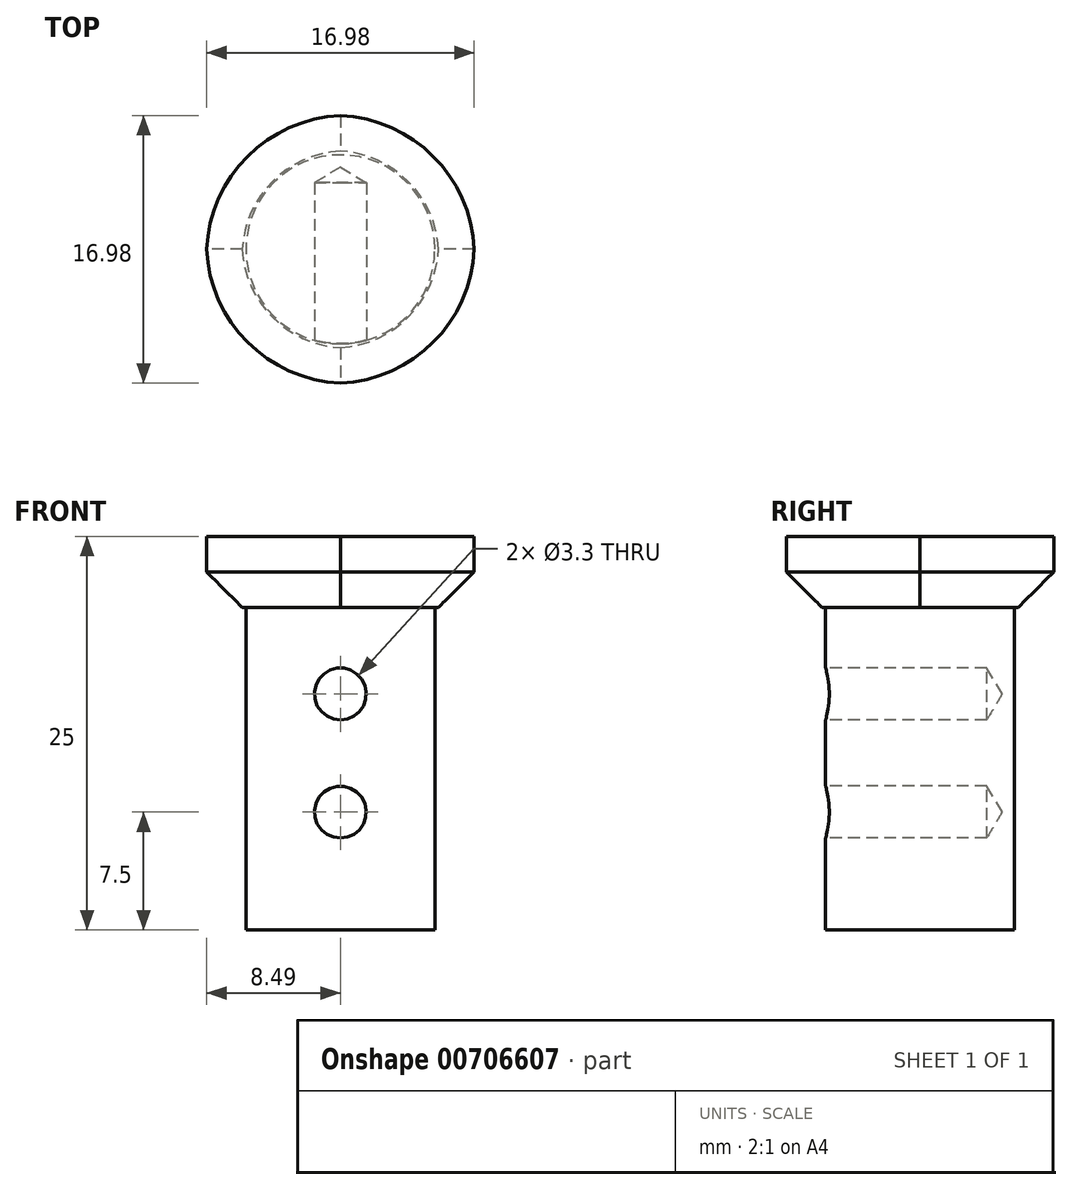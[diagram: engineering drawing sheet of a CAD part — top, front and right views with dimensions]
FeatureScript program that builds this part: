
annotation { "Feature Type Name" : "Feature", "Feature Type Description" : "" }
export const myFeature = defineFeature(function(context is Context, id is Id, definition is map)
    precondition{}
    {
        {
            var Q0;
            Q0=qCreatedBy(makeId("Top.planeOp"),FACE);
            var sketch = newSketch(context, id + "F0", { "sketchPlane" : qUnion([Q0])});
            skLineSegment(sketch, "E0.bottom", {"start": v(8.5, 8.5) * mm, "end": v(-8.5, 8.5) * mm});
            skLineSegment(sketch, "E0.top", {"start": v(8.5, -8.5) * mm, "end": v(-8.5, -8.5) * mm});
            skLineSegment(sketch, "E0.left", {"start": v(8.5, 8.5) * mm, "end": v(8.5, -8.5) * mm});
            skLineSegment(sketch, "E0.right", {"start": v(-8.5, 8.5) * mm, "end": v(-8.5, -8.5) * mm});
            skPoint(sketch, "E0.middle", {"position": v(0, 0) * mm});
            skLineSegment(sketch, "E1.bottom", {"start": v(0, 6) * mm, "end": v(0, 6) * mm});
            skLineSegment(sketch, "E1.top", {"start": v(0, -6) * mm, "end": v(0, -6) * mm});
            skLineSegment(sketch, "E1.left", {"start": v(6, 0) * mm, "end": v(6, 0) * mm});
            skLineSegment(sketch, "E1.right", {"start": v(-6, 0) * mm, "end": v(-6, 0) * mm});
            skPoint(sketch, "E2.visualSharp", {"position": v(-6, -6) * mm});
            skArc(sketch, "E2.filletArc", {"start": v(-6, 0) * mm, "mid": v(-4.24, -4.24) * mm, "end": v(0, -6) * mm});
            skPoint(sketch, "E3.visualSharp", {"position": v(6, -6) * mm});
            skArc(sketch, "E3.filletArc", {"start": v(0, -6) * mm, "mid": v(4.24, -4.24) * mm, "end": v(6, 0) * mm});
            skPoint(sketch, "E4.visualSharp", {"position": v(6, 6) * mm});
            skArc(sketch, "E4.filletArc", {"start": v(6, 0) * mm, "mid": v(4.24, 4.24) * mm, "end": v(0, 6) * mm});
            skPoint(sketch, "E5.visualSharp", {"position": v(-6, 6) * mm});
            skArc(sketch, "E5.filletArc", {"start": v(0, 6) * mm, "mid": v(-4.24, 4.24) * mm, "end": v(-6, 0) * mm});
            skCircle(sketch, "E6", {"center": v(0, 0) * mm, "radius": 8.5 * mm});
            skSolve(sketch);
        }
        {
            var Q0;
            Q0=makeQuery(id+"F0.imprint","IMPRINT",FACE,{"disambiguationData":[TD([[makeQuery(id+"F0.imprint","IMPRINT",EDGE,{"derivedFrom":sQuery(id+"F0.wireOp",EDGE,"E0.bottom")}),1.0]])]});
            var Q1;
            Q1=makeQuery(id+"F0.imprint","IMPRINT",FACE,{"disambiguationData":[TD([[makeQuery(id+"F0.imprint","IMPRINT",EDGE,{"derivedFrom":sQuery(id+"F0.wireOp",EDGE,"E2.filletArc")}),1.0]])]});
            var Q2;
            Q2=makeQuery(id+"F0.imprint","IMPRINT",FACE,{"disambiguationData":[TD([[makeQuery(id+"F0.imprint","IMPRINT",EDGE,{"derivedFrom":sQuery(id+"F0.wireOp",EDGE,"E2.filletArc")}),-1.0]])]});
            var Q3;
            {var subQ0=sQuery(id+"F0.wireOp",EDGE,"E0.right");var subQ1=sQuery(id+"F0.wireOp",EDGE,"E0.top");var subQ2=makeQuery(id+"F0.imprint","INTERSECT",VERTEX,{"derivedFrom":[subQ1,subQ0]});Q3=makeQuery(id+"F0.imprint","IMPRINT",FACE,{"disambiguationData":[TD([[makeQuery(id+"F0.imprint","IMPRINT",EDGE,{"disambiguationData":[TD([[subQ2,1.0]])],"derivedFrom":subQ1}),-1.0]])]});}
            var Q4;
            {var subQ0=sQuery(id+"F0.wireOp",EDGE,"E0.left");var subQ1=sQuery(id+"F0.wireOp",EDGE,"E0.top");var subQ2=makeQuery(id+"F0.imprint","INTERSECT",VERTEX,{"derivedFrom":[subQ1,subQ0]});Q4=makeQuery(id+"F0.imprint","IMPRINT",FACE,{"disambiguationData":[TD([[makeQuery(id+"F0.imprint","IMPRINT",EDGE,{"disambiguationData":[TD([[subQ2,-1.0]])],"derivedFrom":subQ1}),-1.0]])]});}
            extrude(context, id + "F1", {"entities" : qUnion([Q0, Q1, Q2, Q3, Q4]), "depth" : 25 * mm, "offsetDistance" : 25 * mm});
        }
        {
            var Q0;
            Q0=makeQuery(id+"F1.opExtrude","SWEPT_FACE",FACE,{"disambiguationData":[OSD([sQuery(id+"F0.wireOp",EDGE,"E0.top")])]});
            var sketch = newSketch(context, id + "F2", { "sketchPlane" : qUnion([Q0])});
            skLineSegment(sketch, "E7.bottom", {"start": v(-8.5, 0) * mm, "end": v(8.5, 0) * mm});
            skLineSegment(sketch, "E7.top", {"start": v(-8.5, 25) * mm, "end": v(8.5, 25) * mm});
            skLineSegment(sketch, "E7.left", {"start": v(-8.5, 0) * mm, "end": v(-8.5, 25) * mm});
            skLineSegment(sketch, "E7.right", {"start": v(8.5, 0) * mm, "end": v(8.5, 25) * mm});
            skPoint(sketch, "E8", {"position": v(0, 7.5) * mm});
            skPoint(sketch, "E9", {"position": v(0, 15) * mm});
            skPoint(sketch, "E10", {"position": v(0, 10) * mm});
            skPoint(sketch, "E11", {"position": v(0, 17.5) * mm});
            skSolve(sketch);
        }
        {
            var Q0;
            Q0=makeQuery(id+"F1.opExtrude","SWEPT_EDGE",EDGE,{"disambiguationData":[OSD([sQuery(id+"F0.wireOp",EDGE,"E0.top"),sQuery(id+"F0.wireOp",EDGE,"E0.left")])]});
            var Q1;
            Q1=makeQuery(id+"F1.opExtrude","SWEPT_EDGE",EDGE,{"disambiguationData":[OSD([sQuery(id+"F0.wireOp",EDGE,"E0.bottom"),sQuery(id+"F0.wireOp",EDGE,"E0.left")])]});
            var Q2;
            Q2=makeQuery(id+"F1.opExtrude","SWEPT_EDGE",EDGE,{"disambiguationData":[OSD([sQuery(id+"F0.wireOp",EDGE,"E0.top"),sQuery(id+"F0.wireOp",EDGE,"E0.right")])]});
            var Q3;
            Q3=makeQuery(id+"F1.opExtrude","SWEPT_EDGE",EDGE,{"disambiguationData":[OSD([sQuery(id+"F0.wireOp",EDGE,"E0.bottom"),sQuery(id+"F0.wireOp",EDGE,"E0.right")])]});
            fillet(context, id + "F3", {"entities" : qUnion([Q0, Q1, Q2, Q3]), "radius" : 8.88 * mm, "tangentPropagation" : true, "allowEdgeOverflow" : false});
        }
        {
            var Q0;
            Q0=makeQuery(id+"F0.imprint","IMPRINT",FACE,{"disambiguationData":[TD([[makeQuery(id+"F0.imprint","IMPRINT",EDGE,{"derivedFrom":sQuery(id+"F0.wireOp",EDGE,"E2.filletArc")}),-1.0]])]});
            extrude(context, id + "F4", {"entities" : qUnion([Q0]), "operationType" : NewBodyOperationType.REMOVE, "depth" : 20.5 * mm, "offsetDistance" : 25 * mm});
        }
        {
            var Q0;
            Q0=makeQuery(id+"F1.opExtrude","CAP_FACE",FACE,{"disambiguationData":[OSD([sQuery(id+"F0.wireOp",EDGE,"E0.bottom"),sQuery(id+"F0.wireOp",EDGE,"E0.top"),sQuery(id+"F0.wireOp",EDGE,"E0.left"),sQuery(id+"F0.wireOp",EDGE,"E0.right")])],"isStart":false});
            var sketch = newSketch(context, id + "F5", { "sketchPlane" : qUnion([Q0])});
            skLineSegment(sketch, "E12.bottom", {"start": v(8.5, 8.5) * mm, "end": v(-8.5, 8.5) * mm});
            skLineSegment(sketch, "E12.top", {"start": v(8.5, -8.5) * mm, "end": v(-8.5, -8.5) * mm});
            skLineSegment(sketch, "E12.left", {"start": v(8.5, 8.5) * mm, "end": v(8.5, -8.5) * mm});
            skLineSegment(sketch, "E12.right", {"start": v(-8.5, 8.5) * mm, "end": v(-8.5, -8.5) * mm});
            skPoint(sketch, "E12.middle", {"position": v(0, 0) * mm});
            skLineSegment(sketch, "E13.bottom", {"start": v(0, 6) * mm, "end": v(0, 6) * mm});
            skLineSegment(sketch, "E13.top", {"start": v(0, -6) * mm, "end": v(0, -6) * mm});
            skLineSegment(sketch, "E13.left", {"start": v(6, 0) * mm, "end": v(6, 0) * mm});
            skLineSegment(sketch, "E13.right", {"start": v(-6, 0) * mm, "end": v(-6, 0) * mm});
            skPoint(sketch, "E14.visualSharp", {"position": v(-6, -6) * mm});
            skArc(sketch, "E14.filletArc", {"start": v(-6, 0) * mm, "mid": v(-4.24, -4.24) * mm, "end": v(0, -6) * mm});
            skPoint(sketch, "E15.visualSharp", {"position": v(6, -6) * mm});
            skArc(sketch, "E15.filletArc", {"start": v(0, -6) * mm, "mid": v(4.24, -4.24) * mm, "end": v(6, 0) * mm});
            skPoint(sketch, "E16.visualSharp", {"position": v(6, 6) * mm});
            skArc(sketch, "E16.filletArc", {"start": v(6, 0) * mm, "mid": v(4.24, 4.24) * mm, "end": v(0, 6) * mm});
            skPoint(sketch, "E17.visualSharp", {"position": v(-6, 6) * mm});
            skArc(sketch, "E17.filletArc", {"start": v(0, 6) * mm, "mid": v(-4.24, 4.24) * mm, "end": v(-6, 0) * mm});
            skCircle(sketch, "E18", {"center": v(0, 0) * mm, "radius": 8.5 * mm});
            skSolve(sketch);
        }
        {
            var Q0;
            Q0=makeQuery(id+"F4.boolean.opBoolean","INTERSECT",EDGE,{"derivedFrom":[makeQuery(id+"F3.opFillet","BLEND_FACE",FACE,{"disambiguationData":[OSD([sQuery(id+"F0.wireOp",EDGE,"E0.top"),sQuery(id+"F0.wireOp",EDGE,"E0.left")])]}),makeQuery(id+"F4.opExtrude","CAP_FACE",FACE,{"disambiguationData":[OSD([sQuery(id+"F0.wireOp",EDGE,"E2.filletArc"),sQuery(id+"F0.wireOp",EDGE,"E3.filletArc"),sQuery(id+"F0.wireOp",EDGE,"E4.filletArc"),sQuery(id+"F0.wireOp",EDGE,"E5.filletArc"),sQuery(id+"F0.wireOp",EDGE,"E6")])],"isStart":false})]});
            var Q1;
            Q1=makeQuery(id+"F4.boolean.opBoolean","INTERSECT",EDGE,{"derivedFrom":[makeQuery(id+"F3.opFillet","BLEND_FACE",FACE,{"disambiguationData":[OSD([sQuery(id+"F0.wireOp",EDGE,"E0.top"),sQuery(id+"F0.wireOp",EDGE,"E0.right")])]}),makeQuery(id+"F4.opExtrude","CAP_FACE",FACE,{"disambiguationData":[OSD([sQuery(id+"F0.wireOp",EDGE,"E2.filletArc"),sQuery(id+"F0.wireOp",EDGE,"E3.filletArc"),sQuery(id+"F0.wireOp",EDGE,"E4.filletArc"),sQuery(id+"F0.wireOp",EDGE,"E5.filletArc"),sQuery(id+"F0.wireOp",EDGE,"E6")])],"isStart":false})]});
            var Q2;
            Q2=makeQuery(id+"F4.boolean.opBoolean","INTERSECT",EDGE,{"derivedFrom":[makeQuery(id+"F3.opFillet","BLEND_FACE",FACE,{"disambiguationData":[OSD([sQuery(id+"F0.wireOp",EDGE,"E0.bottom"),sQuery(id+"F0.wireOp",EDGE,"E0.left")])]}),makeQuery(id+"F4.opExtrude","CAP_FACE",FACE,{"disambiguationData":[OSD([sQuery(id+"F0.wireOp",EDGE,"E2.filletArc"),sQuery(id+"F0.wireOp",EDGE,"E3.filletArc"),sQuery(id+"F0.wireOp",EDGE,"E4.filletArc"),sQuery(id+"F0.wireOp",EDGE,"E5.filletArc"),sQuery(id+"F0.wireOp",EDGE,"E6")])],"isStart":false})]});
            var Q3;
            Q3=makeQuery(id+"F4.boolean.opBoolean","INTERSECT",EDGE,{"derivedFrom":[makeQuery(id+"F3.opFillet","BLEND_FACE",FACE,{"disambiguationData":[OSD([sQuery(id+"F0.wireOp",EDGE,"E0.bottom"),sQuery(id+"F0.wireOp",EDGE,"E0.right")])]}),makeQuery(id+"F4.opExtrude","CAP_FACE",FACE,{"disambiguationData":[OSD([sQuery(id+"F0.wireOp",EDGE,"E2.filletArc"),sQuery(id+"F0.wireOp",EDGE,"E3.filletArc"),sQuery(id+"F0.wireOp",EDGE,"E4.filletArc"),sQuery(id+"F0.wireOp",EDGE,"E5.filletArc"),sQuery(id+"F0.wireOp",EDGE,"E6")])],"isStart":false})]});
            chamfer(context, id + "F6", {"entities" : qUnion([Q0, Q1, Q2, Q3]), "width" : 2.25 * mm, "tangentPropagation" : true});
        }
        {
            var Q0;
            Q0=sQuery(id+"F2.wireOp",VERTEX,"E8");
            var Q1;
            Q1=sQuery(id+"F2.wireOp",VERTEX,"E9");
            var Q2;
            Q2=makeQuery(id+"F1.opExtrude","SWEPT_BODY",BODY,{"disambiguationData":[OSD([sQuery(id+"F0.wireOp",EDGE,"E0.bottom"),sQuery(id+"F0.wireOp",EDGE,"E0.top"),sQuery(id+"F0.wireOp",EDGE,"E0.left"),sQuery(id+"F0.wireOp",EDGE,"E0.right")])]});
            hole(context, id + "F7", {"style" : HoleStyle.SIMPLE, "endStyle" : HoleEndStyle.BLIND, "standardTappedOrClearance" : lookupTablePath({ "standard" : "ISO", "fit" : "Normal", "size" : "M3", "type" : "Clearance" }), "standardBlindInLast" : lookupTablePath({ "fit" : "Standard", "standard" : "ISO", "size" : "M3", "type" : "Clearance" }), "holeDiameter" : 3.3 * mm, "majorDiameter" : 5 * mm, "holeDepth" : 10 * mm, "isTappedThrough" : true, "tappedDepth" : 12 * mm, "tapClearance" : 3, "locations" : qUnion([Q0, Q1]), "scope" : qUnion([Q2])});
        }
    });
